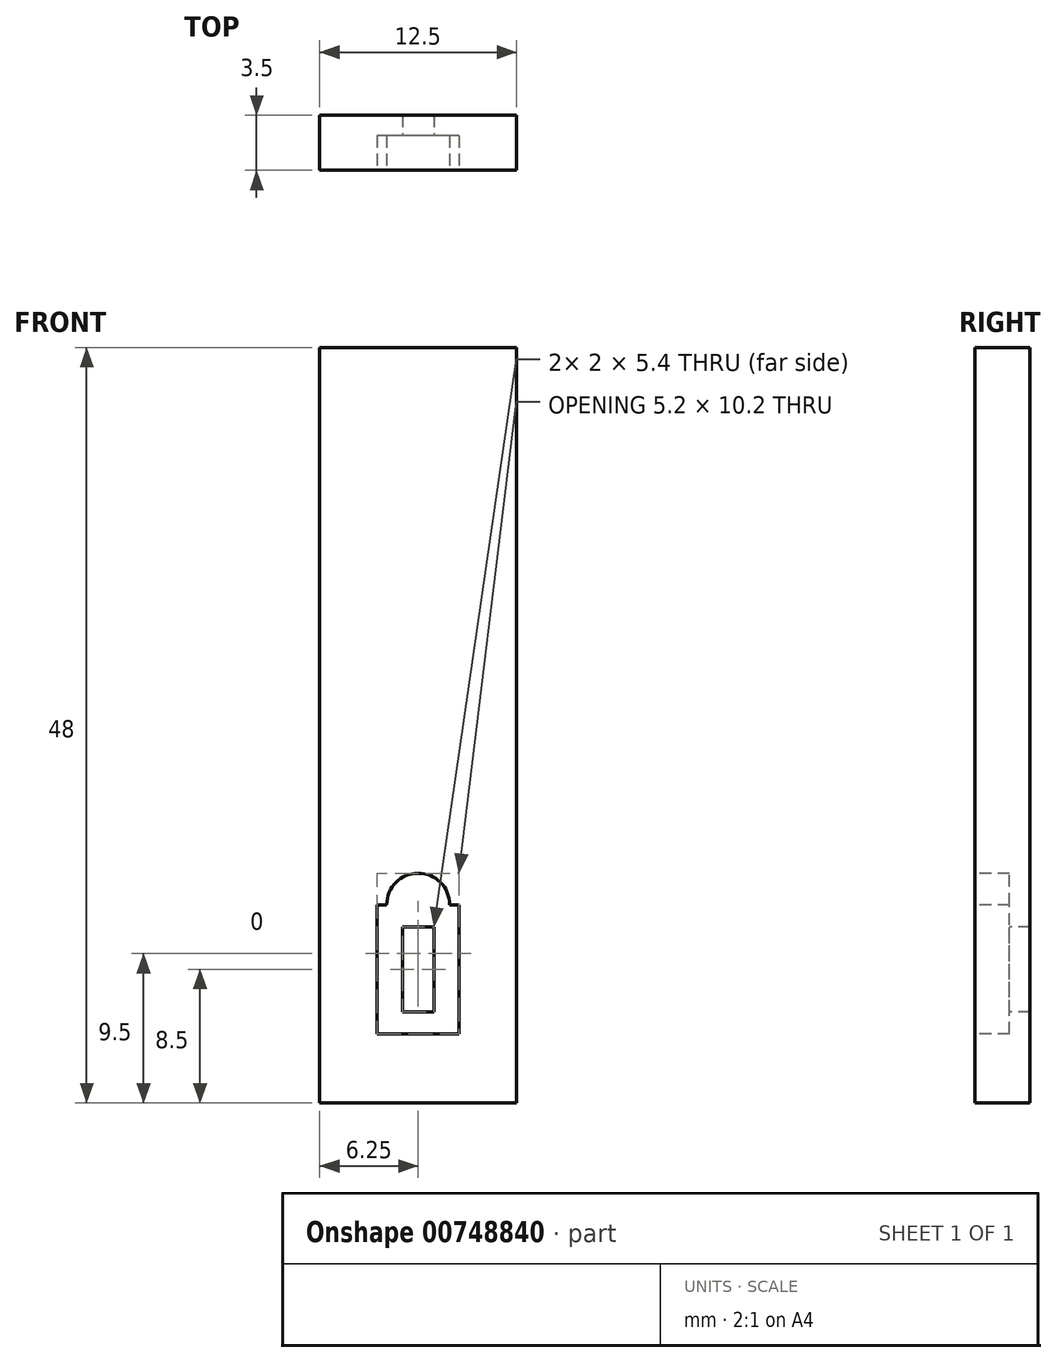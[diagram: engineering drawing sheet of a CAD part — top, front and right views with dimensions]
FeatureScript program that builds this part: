
annotation { "Feature Type Name" : "Feature", "Feature Type Description" : "" }
export const myFeature = defineFeature(function(context is Context, id is Id, definition is map)
    precondition{}
    {
        {
            var Q0;
            Q0=qCreatedBy(makeId("Front.planeOp"),FACE);
            var sketch = newSketch(context, id + "F0", { "sketchPlane" : qUnion([Q0])});
            skLineSegment(sketch, "E0.bottom", {"start": v(6.25, -24) * mm, "end": v(-6.25, -24) * mm});
            skLineSegment(sketch, "E0.top", {"start": v(6.25, 24) * mm, "end": v(-6.25, 24) * mm});
            skLineSegment(sketch, "E0.left", {"start": v(6.25, -24) * mm, "end": v(6.25, 24) * mm});
            skLineSegment(sketch, "E0.right", {"start": v(-6.25, -24) * mm, "end": v(-6.25, 24) * mm});
            skPoint(sketch, "E0.middle", {"position": v(0, 0) * mm});
            skPoint(sketch, "E1.middle.positionSnap0", {"position": v(0, -24) * mm});
            skPoint(sketch, "E1.centerSnap0", {"position": v(0, -24) * mm});
            skSolve(sketch);
        }
        {
            var Q0;
            Q0 = qSketchRegion(id + "F0", true);
            extrude(context, id + "F1", {"entities" : qUnion([Q0]), "oppositeDirection" : true, "depth" : 3.5 * mm, "offsetDistance" : 25 * mm});
        }
        {
            var Q0;
            Q0=qCreatedBy(makeId("Front.planeOp"),FACE);
            var sketch = newSketch(context, id + "F2", { "sketchPlane" : qUnion([Q0])});
            skLineSegment(sketch, "E2.bottom", {"start": v(2.6, -19.6) * mm, "end": v(-2.6, -19.6) * mm});
            skLineSegment(sketch, "E2.top", {"start": v(2.6, -11.4) * mm, "end": v(-2.6, -11.4) * mm});
            skLineSegment(sketch, "E2.left", {"start": v(2.6, -19.6) * mm, "end": v(2.6, -11.4) * mm});
            skLineSegment(sketch, "E2.right", {"start": v(-2.6, -19.6) * mm, "end": v(-2.6, -11.4) * mm});
            skPoint(sketch, "E2.middle", {"position": v(0, -15.5) * mm});
            skSolve(sketch);
        }
        {
            var Q0;
            Q0 = qSketchRegion(id + "F2", true);
            var Q1;
            Q1 = qSketchRegion(id + "F6", true);
            extrude(context, id + "F3", {"entities" : qUnion([Q0, Q1]), "operationType" : NewBodyOperationType.REMOVE, "oppositeDirection" : true, "depth" : 2.2 * mm, "offsetDistance" : 25 * mm});
        }
        {
            var Q0;
            Q0=qCreatedBy(makeId("Front.planeOp"),FACE);
            var sketch = newSketch(context, id + "F4", { "sketchPlane" : qUnion([Q0])});
            skLineSegment(sketch, "E3.bottom", {"start": v(1, -18.2) * mm, "end": v(-1, -18.2) * mm});
            skLineSegment(sketch, "E3.top", {"start": v(1, -12.8) * mm, "end": v(-1, -12.8) * mm});
            skLineSegment(sketch, "E3.left", {"start": v(1, -18.2) * mm, "end": v(1, -12.8) * mm});
            skLineSegment(sketch, "E3.right", {"start": v(-1, -18.2) * mm, "end": v(-1, -12.8) * mm});
            skPoint(sketch, "E3.middle", {"position": v(0, -15.5) * mm});
            skSolve(sketch);
        }
        {
            var Q0;
            Q0 = qSketchRegion(id + "F4", true);
            extrude(context, id + "F5", {"entities" : qUnion([Q0]), "operationType" : NewBodyOperationType.REMOVE, "oppositeDirection" : true, "depth" : 3.5 * mm, "offsetDistance" : 25 * mm});
        }
        {
            var Q0;
            Q0=qCreatedBy(makeId("Front.planeOp"),FACE);
            var sketch = newSketch(context, id + "F6", { "sketchPlane" : qUnion([Q0])});
            skCircle(sketch, "E4", {"center": v(0, -11.4) * mm, "radius": 2 * mm});
            skSolve(sketch);
        }
        {
            var Q0;
            Q0 = qSketchRegion(id + "F6", true);
            extrude(context, id + "F7", {"entities" : qUnion([Q0]), "operationType" : NewBodyOperationType.REMOVE, "oppositeDirection" : true, "depth" : 2.2 * mm, "offsetDistance" : 25 * mm});
        }
    });
